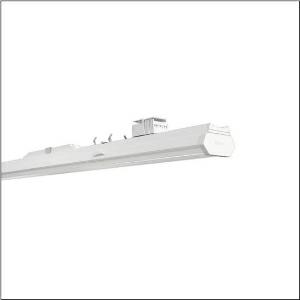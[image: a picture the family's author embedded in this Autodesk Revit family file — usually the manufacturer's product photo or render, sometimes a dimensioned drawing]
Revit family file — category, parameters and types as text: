
# Revit family: licross_21_protected_ho_52tp12dn4e5m3c
name_source: partatom
category: Lighting Fixtures
units: mm (PartAtom-declared; Revit-internal decimal feet)

## family parameters
Cut with Voids When Loaded = No
Host = Face
Light Source = No
Part Type = Normal
Room Calculation Point = No
Round Connector Dimension = Use Diameter
Shared = No

## types (1)
- --- (1 x LED, 910 lm, 7.6 W, 4000K)
    Apparent Load = 8 VA
    CIE Flux Codes = 70 91 97 98 100
    Color Rendering = 80
    Color Temperature = 4000K
    Default Elevation = 1800 mm
    Description = Licross 21 Protected HO, luminaire insert, of sheet steel, galvanised, coil coated, white, length: 1.500mm, width: 90mm, height: 103mm, LED rated luminous flux: 14.690lm, light colour: 840, SDCM (Standard Deviation of Colour Matching)MacAdam ≤ 3 SDCM (initial), control gear: DALI 2 (for two DALI lines), with plug, 6-pole, with phase selection, for trunking rail, 14-core, mains connection: 220..240V, AC, 50/60Hz, rated input power: 89W, for trunking rail, 14-core, internal wiring halogen-free, for emergency light function, converter,control gear: single battery element, battery: LiFePO4, 9Ah, primary light control with lens, of plastic, primary optical cover: cover, of PMMA, light emission: direct distribution, primary light characteristic: symmetric, protection rating (complete): IP64, insulation class (complete): insulation class I (protective earthing), certification: CE, UKCA, protection symbol: D if used in an environment with conductive dust loads with corresponding accessories, impact resistance: IK06, permissible ambient temperature for indoor applications: +5..+30°C, standard: EN 60598-2-22, LABS conformity tested according to VDMA 24364:2018-05, reducing of maximum allowable ambient temperature of 5°C with ceiling mounting, corresponds to IFS (International Featured Standards) requirements for safety and quality in the food industry, The light source and the operating device comply with the requirements of the Ecodesign Regulation (EU) 2019/2020 and are replaceable in accordance with this regulation, packaging unit: 1 piece
    Height = 92 mm
    Lamp = 1 x LED
    Lamp Light Flux = 910 lm
    Lamp Power = 7.6 W
    Lamp count = 1
    Length = 1500 mm
    Luminous efficacy = 120 lm/W
    Manufacturer = Siteco
    ModVariant = No
    Model = 52TP12DN4E5M3C
    Mounting Place = Ceiling
    Mounting Type = Pendant
    Number of Poles = 1
    OnlyDefault = Yes
    Power Factor = 1
    Product Name = Licross 21 Protected HO
    Product group = luminaire insert | ceiling pendant
    ProductGroupID = 901
    Protection Class = Protection class I
    Protection Degree = IP 64
    RLX_Detail_Level = 1
    RLX_Emergency_Light_Flux = 0 lm
    RLX_Emergency_Type = 0
    RLX_Emergency_Type_DB = No
    RlxData = <blob elided: 25133 chars, md5=57c66c6e>
    Socket = socket
    Standby Power = 0 W
    System Light Flux = 910 lm
    System Power = 8 W
    Type Comments = : emergency light operation: 3 h
    Type Image = l_1256148.jpg
    URL = http://relux.com
    VarID = @adj_111173
    Voltage = 0 V
    Weight = 0.00 kg
    Width = 88 mm

## geometry (parser evidence)
native form markers: Blend x4, Sweep x12
no freeform markers — native parametric forms only
